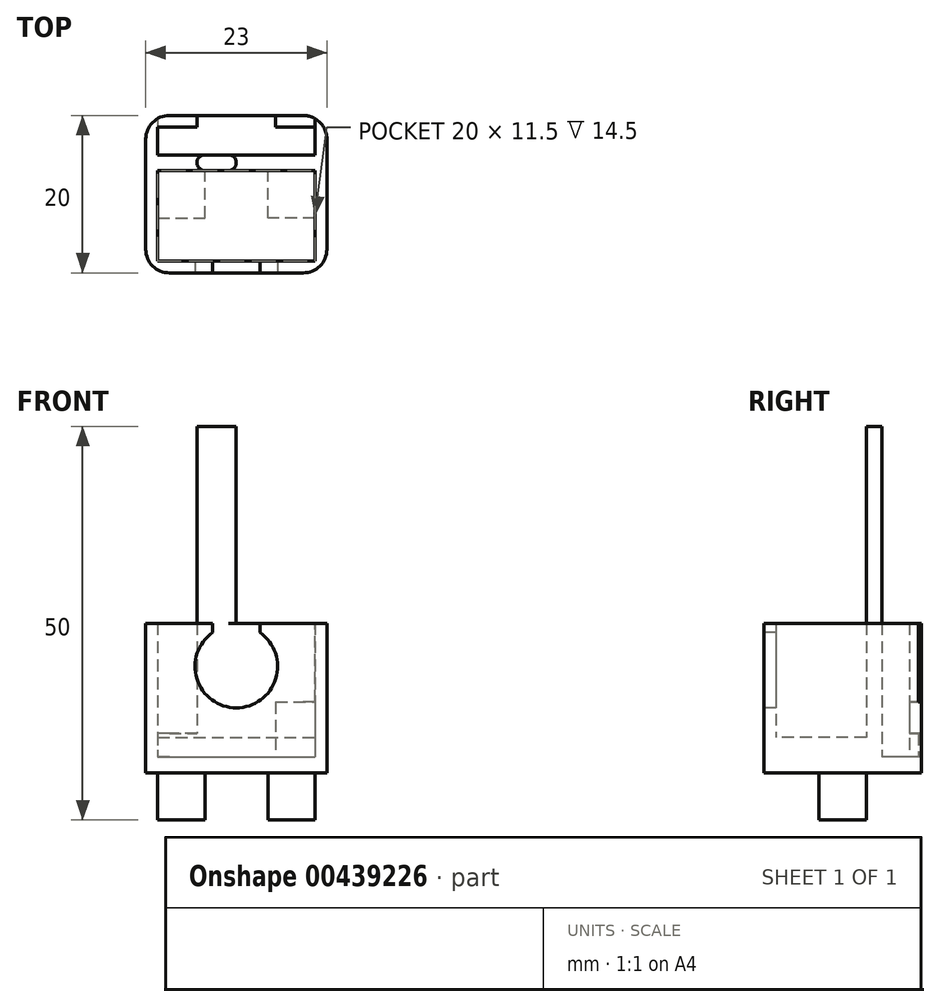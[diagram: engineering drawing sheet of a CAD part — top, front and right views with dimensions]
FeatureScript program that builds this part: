
annotation { "Feature Type Name" : "Feature", "Feature Type Description" : "" }
export const myFeature = defineFeature(function(context is Context, id is Id, definition is map)
    precondition{}
    {
        {
            var Q0;
            Q0=qCreatedBy(makeId("Top.planeOp"),FACE);
            var sketch = newSketch(context, id + "F0", { "sketchPlane" : qUnion([Q0])});
            skLineSegment(sketch, "E0.bottom", {"start": v(11.5, -7) * mm, "end": v(-11.5, -7) * mm});
            skLineSegment(sketch, "E0.top", {"start": v(11.5, 7) * mm, "end": v(-11.5, 7) * mm});
            skLineSegment(sketch, "E0.left", {"start": v(11.5, -7) * mm, "end": v(11.5, 7) * mm});
            skLineSegment(sketch, "E0.right", {"start": v(-11.5, -7) * mm, "end": v(-11.5, 7) * mm});
            skPoint(sketch, "E0.middle", {"position": v(0, 0) * mm});
            skLineSegment(sketch, "E1.bottom", {"start": v(-11.5, 7) * mm, "end": v(11.5, 7) * mm, "construction": true});
            skLineSegment(sketch, "E1.top", {"start": v(-11.5, 13) * mm, "end": v(-5, 13) * mm});
            skLineSegment(sketch, "E1.left", {"start": v(-11.5, 7) * mm, "end": v(-11.5, 13) * mm});
            skLineSegment(sketch, "E1.right", {"start": v(11.5, 7) * mm, "end": v(11.5, 13) * mm});
            skLineSegment(sketch, "E2", {"start": v(-5, 13) * mm, "end": v(-5, 11.5) * mm});
            skLineSegment(sketch, "E3", {"start": v(-5, 11.5) * mm, "end": v(-10, 11.5) * mm});
            skLineSegment(sketch, "E4", {"start": v(-10, 11.5) * mm, "end": v(-10, 8) * mm});
            skLineSegment(sketch, "E5", {"start": v(-10, 8) * mm, "end": v(0, 8) * mm});
            skLineSegment(sketch, "E6", {"start": v(0, 6) * mm, "end": v(-10, 6) * mm});
            skLineSegment(sketch, "E7", {"start": v(-10, 6) * mm, "end": v(-10, -5.5) * mm});
            skLineSegment(sketch, "E8", {"start": v(-10, -5.5) * mm, "end": v(0, -5.5) * mm});
            skLineSegment(sketch, "E9.MirrorCS", {"start": v(5, 13) * mm, "end": v(5, 11.5) * mm});
            skLineSegment(sketch, "E10.MirrorCS", {"start": v(5, 11.5) * mm, "end": v(10, 11.5) * mm});
            skLineSegment(sketch, "E11.MirrorCS", {"start": v(10, 11.5) * mm, "end": v(10, 8) * mm});
            skLineSegment(sketch, "E12.MirrorCS", {"start": v(10, 8) * mm, "end": v(0, 8) * mm});
            skLineSegment(sketch, "E13.MirrorCS", {"start": v(0, 6) * mm, "end": v(10, 6) * mm});
            skLineSegment(sketch, "E14.MirrorCS", {"start": v(10, 6) * mm, "end": v(10, -5.5) * mm});
            skLineSegment(sketch, "E15.MirrorCS", {"start": v(10, -5.5) * mm, "end": v(0, -5.5) * mm});
            skLineSegment(sketch, "E16.trimOffspring", {"start": v(5, 13) * mm, "end": v(11.5, 13) * mm});
            skLineSegment(sketch, "E17", {"start": v(-5, 11.5) * mm, "end": v(5, 11.5) * mm});
            skLineSegment(sketch, "E18", {"start": v(-5, 13) * mm, "end": v(5, 13) * mm});
            skLineSegment(sketch, "E19", {"start": v(-10, 11.5) * mm, "end": v(-10, 13) * mm});
            skSolve(sketch);
        }
        {
            var Q0;
            Q0=makeQuery(id+"F0.imprint","IMPRINT",FACE,{"disambiguationData":[TD([[makeQuery(id+"F0.imprint","IMPRINT",EDGE,{"derivedFrom":sQuery(id+"F0.wireOp",EDGE,"E0.bottom")}),-1.0]])]});
            var Q1;
            Q1=makeQuery(id+"F0.imprint","IMPRINT",FACE,{"disambiguationData":[TD([[makeQuery(id+"F0.imprint","IMPRINT",EDGE,{"derivedFrom":sQuery(id+"F0.wireOp",EDGE,"E0.top")}),-1.0]])]});
            extrude(context, id + "F1", {"entities" : qUnion([Q0, Q1]), "depth" : 19 * mm, "offsetDistance" : 25 * mm});
        }
        {
            var Q0;
            Q0=makeQuery(id+"F0.imprint","IMPRINT",FACE,{"disambiguationData":[TD([[makeQuery(id+"F0.imprint","IMPRINT",EDGE,{"derivedFrom":sQuery(id+"F0.wireOp",EDGE,"E6")}),1.0]])]});
            var Q1;
            Q1=makeQuery(id+"F0.imprint","IMPRINT",FACE,{"disambiguationData":[TD([[makeQuery(id+"F0.imprint","IMPRINT",EDGE,{"derivedFrom":sQuery(id+"F0.wireOp",EDGE,"E3")}),1.0]])]});
            var Q2;
            Q2=makeQuery(id+"F0.imprint","IMPRINT",FACE,{"disambiguationData":[TD([[makeQuery(id+"F0.imprint","IMPRINT",EDGE,{"derivedFrom":sQuery(id+"F0.wireOp",EDGE,"E2")}),1.0]])]});
            extrude(context, id + "F2", {"entities" : qUnion([Q0, Q1, Q2]), "operationType" : NewBodyOperationType.ADD, "depth" : 2 * mm, "offsetDistance" : 25 * mm});
        }
        {
            var Q0;
            Q0=makeQuery(id+"F1.opExtrude","SWEPT_FACE",FACE,{"disambiguationData":[OSD([sQuery(id+"F0.wireOp",EDGE,"E0.bottom")])]});
            var sketch = newSketch(context, id + "F3", { "sketchPlane" : qUnion([Q0])});
            skArc(sketch, "E20", {"start": v(-3, 17.8) * mm, "mid": v(0, 8.25) * mm, "end": v(3, 17.8) * mm});
            skLineSegment(sketch, "E21", {"start": v(-3, 19) * mm, "end": v(-3, 17.8) * mm});
            skLineSegment(sketch, "E22.MirrorCS", {"start": v(3, 19) * mm, "end": v(3, 17.8) * mm});
            skSolve(sketch);
        }
        {
            var Q0;
            Q0=makeQuery(id+"F1.opExtrude","CAP_FACE",FACE,{"disambiguationData":[OSD([sQuery(id+"F0.wireOp",EDGE,"E0.bottom"),sQuery(id+"F0.wireOp",EDGE,"E0.left"),sQuery(id+"F0.wireOp",EDGE,"E0.right"),sQuery(id+"F0.wireOp",EDGE,"E1.top"),sQuery(id+"F0.wireOp",EDGE,"E1.left"),sQuery(id+"F0.wireOp",EDGE,"E1.right"),sQuery(id+"F0.wireOp",EDGE,"E2"),sQuery(id+"F0.wireOp",EDGE,"E3"),sQuery(id+"F0.wireOp",EDGE,"E4"),sQuery(id+"F0.wireOp",EDGE,"E5"),sQuery(id+"F0.wireOp",EDGE,"E6"),sQuery(id+"F0.wireOp",EDGE,"E7"),sQuery(id+"F0.wireOp",EDGE,"E8"),sQuery(id+"F0.wireOp",EDGE,"E9.MirrorCS"),sQuery(id+"F0.wireOp",EDGE,"E10.MirrorCS"),sQuery(id+"F0.wireOp",EDGE,"E11.MirrorCS"),sQuery(id+"F0.wireOp",EDGE,"E12.MirrorCS"),sQuery(id+"F0.wireOp",EDGE,"E13.MirrorCS"),sQuery(id+"F0.wireOp",EDGE,"E14.MirrorCS"),sQuery(id+"F0.wireOp",EDGE,"E15.MirrorCS"),sQuery(id+"F0.wireOp",EDGE,"E16.trimOffspring")])],"isStart":false});
            var sketch = newSketch(context, id + "F4", { "sketchPlane" : qUnion([Q0])});
            skLineSegment(sketch, "E23", {"start": v(10, 8) * mm, "end": v(10, 6) * mm});
            skLineSegment(sketch, "E24", {"start": v(0, 8) * mm, "end": v(0, 6) * mm});
            skLineSegment(sketch, "E25", {"start": v(10, 11.5) * mm, "end": v(10, 13) * mm});
            skLineSegment(sketch, "E26", {"start": v(-5, 8) * mm, "end": v(-5, 6) * mm});
            skSolve(sketch);
        }
        {
            var Q0;
            {var subQ0=sQuery(id+"F4.wireOp",EDGE,"E25");Q0=makeQuery(id+"F4.imprint","IMPRINT",FACE,{"disambiguationData":[TD([[makeQuery(id+"F4.imprint","IMPRINT",EDGE,{"derivedFrom":subQ0}),1.0]])]});}
            extrude(context, id + "F5", {"entities" : qUnion([Q0]), "operationType" : NewBodyOperationType.REMOVE, "oppositeDirection" : true, "depth" : 10 * mm, "offsetDistance" : 25 * mm});
        }
        {
            var Q0;
            Q0=makeQuery(id+"F2.opExtrude","CAP_FACE",FACE,{"disambiguationData":[OSD([sQuery(id+"F0.wireOp",EDGE,"E6"),sQuery(id+"F0.wireOp",EDGE,"E7"),sQuery(id+"F0.wireOp",EDGE,"E8"),sQuery(id+"F0.wireOp",EDGE,"E13.MirrorCS"),sQuery(id+"F0.wireOp",EDGE,"E14.MirrorCS"),sQuery(id+"F0.wireOp",EDGE,"E15.MirrorCS")])],"isStart":false});
            extrude(context, id + "F6", {"entities" : qUnion([Q0]), "operationType" : NewBodyOperationType.ADD, "depth" : 2.5 * mm, "offsetDistance" : 25 * mm});
        }
        {
            var Q0;
            {var subQ0=sQuery(id+"F3.wireOp",EDGE,"E20");var subQ1=makeQuery(id+"F1.opExtrude","CAP_EDGE",EDGE,{"disambiguationData":[OSD([sQuery(id+"F0.wireOp",EDGE,"E0.bottom")])],"isStart":false});var subQ2=makeQuery(id+"F3.imprint","INTERSECT",VERTEX,{"disambiguationData":[OD(0.0)],"derivedFrom":[subQ1,subQ0]});Q0=makeQuery(id+"F3.imprint","IMPRINT",FACE,{"disambiguationData":[TD([[makeQuery(id+"F3.imprint","IMPRINT",EDGE,{"disambiguationData":[TD([[subQ2,1.0]])],"derivedFrom":subQ0}),1.0]])]});}
            extrude(context, id + "F7", {"entities" : qUnion([Q0]), "operationType" : NewBodyOperationType.REMOVE, "oppositeDirection" : true, "depth" : 3 * mm, "offsetDistance" : 25 * mm});
        }
        {
            var Q0;
            {var subQ0=sQuery(id+"F0.wireOp",EDGE,"E2");Q0=makeQuery(id+"F0.imprint","IMPRINT",FACE,{"disambiguationData":[TD([[makeQuery(id+"F0.imprint","IMPRINT",EDGE,{"derivedFrom":subQ0}),-1.0]])]});}
            extrude(context, id + "F8", {"entities" : qUnion([Q0]), "operationType" : NewBodyOperationType.ADD, "depth" : 19 * mm, "offsetDistance" : 25 * mm, "hasSecondDirection" : true, "secondDirectionOppositeDirection" : false, "secondDirectionDepth" : 5 * mm});
        }
        {
            var Q0;
            {var subQ0=sQuery(id+"F0.wireOp",EDGE,"E2");Q0=makeQuery(id+"F0.imprint","IMPRINT",FACE,{"disambiguationData":[TD([[makeQuery(id+"F0.imprint","IMPRINT",EDGE,{"derivedFrom":subQ0}),-1.0]])]});}
            extrude(context, id + "F9", {"entities" : qUnion([Q0]), "operationType" : NewBodyOperationType.ADD, "depth" : 2 * mm, "offsetDistance" : 25 * mm});
        }
        {
            var Q0;
            Q0=makeQuery(id+"F1.opExtrude","SWEPT_EDGE",EDGE,{"disambiguationData":[OSD([sQuery(id+"F0.wireOp",EDGE,"E0.bottom"),sQuery(id+"F0.wireOp",EDGE,"E0.left")])]});
            var Q1;
            Q1=makeQuery(id+"F1.opExtrude","SWEPT_EDGE",EDGE,{"disambiguationData":[OSD([sQuery(id+"F0.wireOp",EDGE,"E0.bottom"),sQuery(id+"F0.wireOp",EDGE,"E0.right")])]});
            var Q2;
            Q2=makeQuery(id+"F1.opExtrude","SWEPT_EDGE",EDGE,{"disambiguationData":[OSD([sQuery(id+"F0.wireOp",EDGE,"E1.right"),sQuery(id+"F0.wireOp",EDGE,"E16.trimOffspring")])]});
            var Q3;
            Q3=makeQuery(id+"F1.opExtrude","SWEPT_EDGE",EDGE,{"disambiguationData":[OSD([sQuery(id+"F0.wireOp",EDGE,"E1.top"),sQuery(id+"F0.wireOp",EDGE,"E1.left")])]});
            fillet(context, id + "F10", {"entities" : qUnion([Q0, Q1, Q2, Q3]), "radius" : 3 * mm, "tangentPropagation" : true, "allowEdgeOverflow" : false});
        }
        {
            var Q0;
            {var subQ0=sQuery(id+"F4.wireOp",EDGE,"E24");Q0=makeQuery(id+"F4.imprint","IMPRINT",FACE,{"disambiguationData":[TD([[makeQuery(id+"F4.imprint","IMPRINT",EDGE,{"derivedFrom":subQ0}),-1.0]])]});}
            extrude(context, id + "F11", {"entities" : qUnion([Q0]), "operationType" : NewBodyOperationType.ADD, "depth" : 25 * mm, "offsetDistance" : 25 * mm});
        }
        {
            var Q0;
            Q0=makeQuery(id+"F11.opExtrude","SWEPT_EDGE",EDGE,{"disambiguationData":[OSD([sQuery(id+"F0.wireOp",EDGE,"E6"),sQuery(id+"F0.wireOp",EDGE,"E13.MirrorCS"),sQuery(id+"F4.wireOp",EDGE,"E24")])]});
            var Q1;
            Q1=makeQuery(id+"F11.opExtrude","SWEPT_EDGE",EDGE,{"disambiguationData":[OSD([sQuery(id+"F0.wireOp",EDGE,"E5"),sQuery(id+"F0.wireOp",EDGE,"E12.MirrorCS"),sQuery(id+"F4.wireOp",EDGE,"E24")])]});
            var Q2;
            Q2=makeQuery(id+"F11.opExtrude","SWEPT_EDGE",EDGE,{"disambiguationData":[OSD([sQuery(id+"F0.wireOp",EDGE,"E6"),sQuery(id+"F0.wireOp",EDGE,"E13.MirrorCS"),sQuery(id+"F4.wireOp",EDGE,"E26")])]});
            var Q3;
            Q3=makeQuery(id+"F11.opExtrude","SWEPT_EDGE",EDGE,{"disambiguationData":[OSD([sQuery(id+"F0.wireOp",EDGE,"E5"),sQuery(id+"F0.wireOp",EDGE,"E12.MirrorCS"),sQuery(id+"F4.wireOp",EDGE,"E26")])]});
            fillet(context, id + "F12", {"entities" : qUnion([Q0, Q1, Q2, Q3]), "radius" : 1 * mm, "tangentPropagation" : true, "allowEdgeOverflow" : false});
        }
        {
            var Q0;
            Q0=makeQuery(id+"F0.imprint","IMPRINT",FACE,{"disambiguationData":[TD([[makeQuery(id+"F0.imprint","IMPRINT",EDGE,{"derivedFrom":sQuery(id+"F0.wireOp",EDGE,"E6")}),1.0]])]});
            cPlane(context, id + "F13", {"entities" : qUnion([Q0]), "cplaneType" : CPlaneType.OFFSET, "offset" : 0 * mm, "width" : 150 * mm, "height" : 150 * mm});
        }
        {
            var Q0;
            Q0=qCreatedBy(id+"F13.planeOp",FACE);
            var Q1;
            Q1=qCreatedBy(id+"F13.planeOp",FACE);
            var Q2;
            Q2=makeQuery(id+"F0.imprint","IMPRINT",FACE,{"disambiguationData":[TD([[makeQuery(id+"F0.imprint","IMPRINT",EDGE,{"derivedFrom":sQuery(id+"F0.wireOp",EDGE,"E6")}),1.0]])]});
            var sketch = newSketch(context, id + "F14", { "sketchPlane" : qUnion([Q0, Q1, Q2])});
            skLineSegment(sketch, "E27.bottom", {"start": v(-10, 0) * mm, "end": v(-4, 0) * mm});
            skLineSegment(sketch, "E27.top", {"start": v(-10, 6) * mm, "end": v(-4, 6) * mm});
            skLineSegment(sketch, "E27.left", {"start": v(-10, 0) * mm, "end": v(-10, 6) * mm});
            skLineSegment(sketch, "E27.right", {"start": v(-4, 0) * mm, "end": v(-4, 6) * mm});
            skLineSegment(sketch, "E28", {"start": v(-4, 0) * mm, "end": v(0, 0) * mm, "construction": true});
            skLineSegment(sketch, "E29.MirrorCS", {"start": v(4, 0) * mm, "end": v(4, 6) * mm});
            skLineSegment(sketch, "E30.MirrorCS", {"start": v(10, 0) * mm, "end": v(4, 0) * mm});
            skLineSegment(sketch, "E31.MirrorCS", {"start": v(10, 0) * mm, "end": v(10, 6) * mm});
            skLineSegment(sketch, "E32.MirrorCS", {"start": v(10, 6) * mm, "end": v(4, 6) * mm});
            skLineSegment(sketch, "E33", {"start": v(-5.86, 0) * mm, "end": v(-5.93, -7) * mm, "construction": true});
            skSolve(sketch);
        }
        {
            var Q0;
            Q0=makeQuery(id+"F14.imprint","IMPRINT",FACE,{"disambiguationData":[TD([[makeQuery(id+"F14.imprint","IMPRINT",EDGE,{"derivedFrom":sQuery(id+"F14.wireOp",EDGE,"E27.bottom")}),1.0]])]});
            var Q1;
            Q1=makeQuery(id+"F14.imprint","IMPRINT",FACE,{"disambiguationData":[TD([[makeQuery(id+"F14.imprint","IMPRINT",EDGE,{"derivedFrom":sQuery(id+"F14.wireOp",EDGE,"E29.MirrorCS")}),-1.0]])]});
            extrude(context, id + "F15", {"entities" : qUnion([Q0, Q1]), "operationType" : NewBodyOperationType.ADD, "oppositeDirection" : true, "depth" : 6 * mm, "offsetDistance" : 25 * mm});
        }
    });
